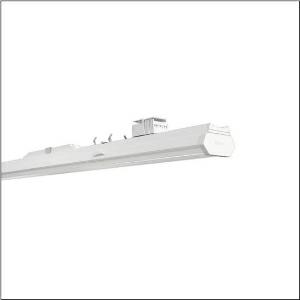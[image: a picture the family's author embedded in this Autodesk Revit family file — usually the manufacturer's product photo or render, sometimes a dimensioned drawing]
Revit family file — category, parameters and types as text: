
# Revit family: licross_r__11_protected_ho_51tp13dn4exr_e985
name_source: partatom
category: Lighting Fixtures
units: mm (PartAtom-declared; Revit-internal decimal feet)

## family parameters
Cut with Voids When Loaded = No
Host = Face
Light Source = No
Part Type = Normal
Room Calculation Point = No
Round Connector Dimension = Use Diameter
Shared = No

## types (1)
- --- (1 x LED, 14170 lm, 84.2 W, 4000K)
    Apparent Load = 84 VA
    CIE Flux Codes = 89 96 99 100 99
    Color Rendering = 80
    Color Temperature = 4000K
    Default Elevation = 1800 mm
    Description = Licross® 11 Protected HOluminaire insert, length: 1.500mm, width: 90mm, height: 101mm, LED rated luminous flux: 14.170lm, light colour: 840, control gear: DALI 2, control gear: ECG DALI, with plug, 5-pole, with phase selection, mains connection: 220..240V, AC, 50/60Hz, halogen-free wiring, primary optical cover: cover, of PMMA, light emission: direct distribution, protection rating (complete): IP64, insulation class (complete): insulation class I (protective earthing), certification: CE, ENEC, VDE, protection symbol: D if used in an environment with conductive dust loads with corresponding accessories, permissible ambient temperature for indoor applications: -25..+35°C, reducing of maximum allowable ambient temperature of 5°C with ceiling mounting, corresponds to IFS (International Featured Standards) requirements for safety and quality in the food industry, packaging unit: 1 piece
    Height = 92 mm
    Lamp = 1 x LED
    Lamp Light Flux = 14170 lm
    Lamp Power = 84.2 W
    Lamp count = 1
    Length = 1500 mm
    Luminous efficacy = 168 lm/W
    Manufacturer = Siteco
    ModVariant = No
    Model = 51TP13DN4EXR
    Mounting Place = Ceiling
    Mounting Type = Pendant
    Number of Poles = 1
    OnlyDefault = Yes
    Power Factor = 1
    Product Name = Licross® 11 Protected HO
    Product group = luminaire insert
    ProductGroupID = 902
    Protection Class = Protection class I
    Protection Degree = IP 64
    RLX_Detail_Level = 1
    RlxData = <blob elided: 23905 chars, md5=7d246275>
    Socket = socket
    Standby Power = 0 W
    System Light Flux = 14170 lm
    System Power = 84 W
    Type Comments = factory setting: luminous flux: 100 % | dim-lin: 254 | 475 mA
    Type Image = l_1256148.jpg
    URL = http://relux.com
    VarID = @adj_137565
    Voltage = 0 V
    Weight = 0.00 kg
    Width = 88 mm

## geometry (parser evidence)
native form markers: Blend x4, Sweep x12
no freeform markers — native parametric forms only
